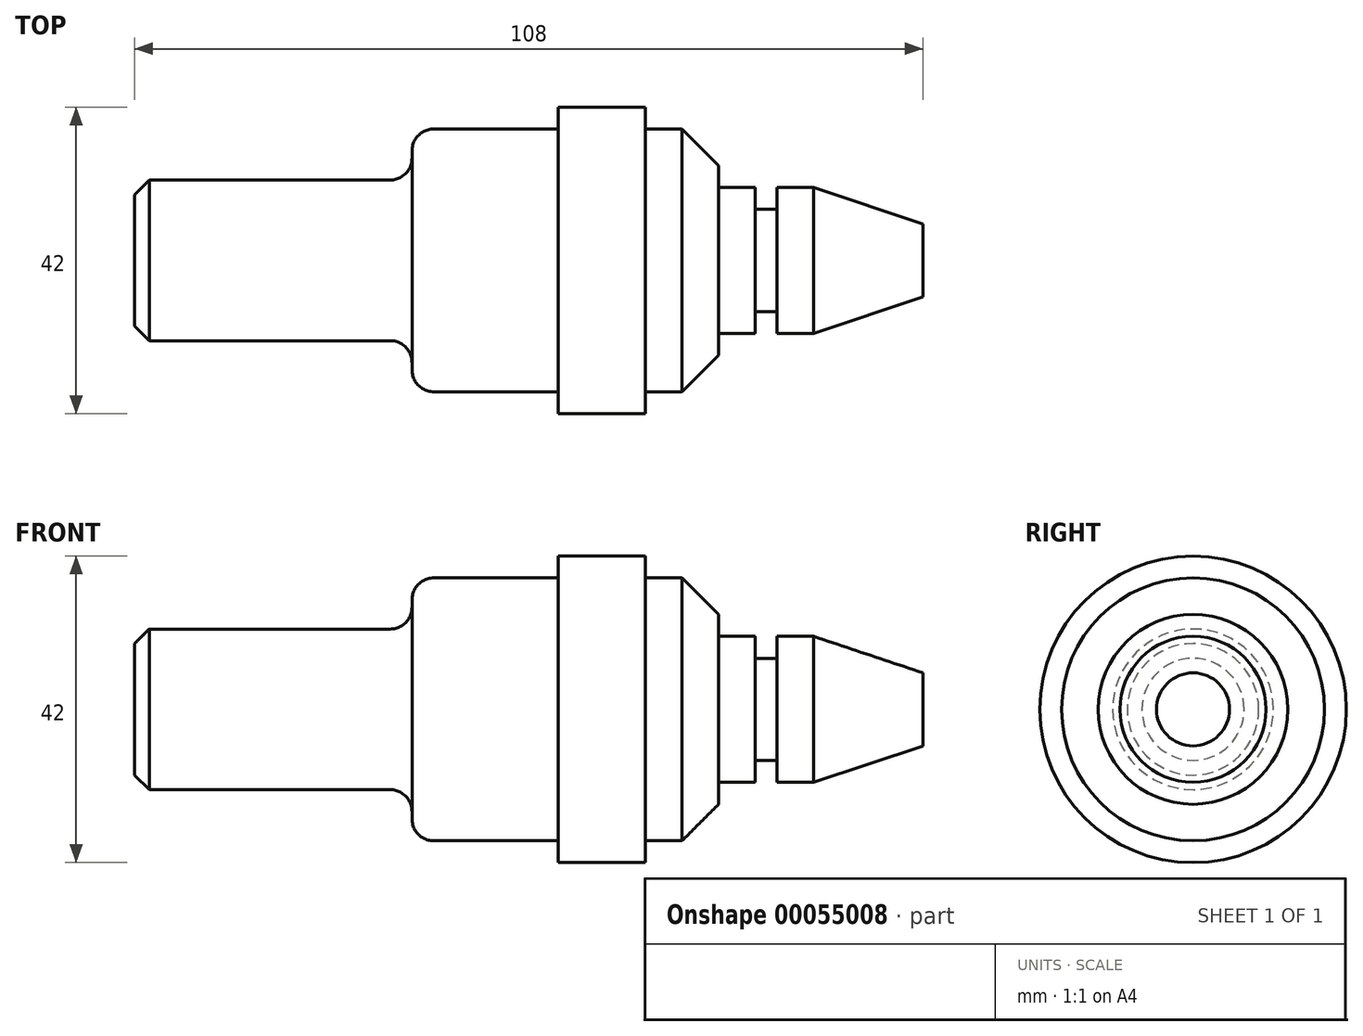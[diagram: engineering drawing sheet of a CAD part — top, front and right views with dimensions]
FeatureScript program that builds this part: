
annotation { "Feature Type Name" : "Feature", "Feature Type Description" : "" }
export const myFeature = defineFeature(function(context is Context, id is Id, definition is map)
    precondition{}
    {
        {
            var Q0;
            Q0=qCreatedBy(makeId("Top.planeOp"),FACE);
            var sketch = newSketch(context, id + "F0", { "sketchPlane" : qUnion([Q0])});
            skLineSegment(sketch, "E0", {"start": v(-39.66, 0) * mm, "end": v(68.34, 0) * mm});
            skLineSegment(sketch, "E1", {"start": v(-39.66, 0) * mm, "end": v(-39.66, -11) * mm});
            skLineSegment(sketch, "E2", {"start": v(-39.66, -11) * mm, "end": v(-1.66, -11) * mm});
            skLineSegment(sketch, "E3", {"start": v(-1.66, -11) * mm, "end": v(-1.66, -18) * mm});
            skLineSegment(sketch, "E4", {"start": v(-1.66, -18) * mm, "end": v(18.34, -18) * mm});
            skLineSegment(sketch, "E5", {"start": v(18.34, -18) * mm, "end": v(18.34, -21) * mm});
            skLineSegment(sketch, "E6", {"start": v(18.34, -21) * mm, "end": v(30.34, -21) * mm});
            skLineSegment(sketch, "E7", {"start": v(30.34, -21) * mm, "end": v(30.34, -18) * mm});
            skLineSegment(sketch, "E8", {"start": v(30.34, -18) * mm, "end": v(40.34, -18) * mm});
            skLineSegment(sketch, "E9", {"start": v(40.34, -18) * mm, "end": v(40.34, -10) * mm});
            skLineSegment(sketch, "E10", {"start": v(40.34, -10) * mm, "end": v(45.34, -10) * mm});
            skLineSegment(sketch, "E11", {"start": v(45.34, -10) * mm, "end": v(45.34, -7) * mm});
            skLineSegment(sketch, "E12", {"start": v(45.34, -7) * mm, "end": v(48.34, -7) * mm});
            skLineSegment(sketch, "E13", {"start": v(48.34, -7) * mm, "end": v(48.34, -10) * mm});
            skLineSegment(sketch, "E14", {"start": v(48.34, -10) * mm, "end": v(53.34, -10) * mm});
            skLineSegment(sketch, "E15", {"start": v(53.34, -10) * mm, "end": v(68.34, -5) * mm});
            skLineSegment(sketch, "E16", {"start": v(68.34, 0) * mm, "end": v(68.34, -5) * mm});
            skSolve(sketch);
        }
        {
            var Q0;
            Q0=makeQuery(id+"F0.imprint","IMPRINT",FACE,{"disambiguationData":[TD([[makeQuery(id+"F0.imprint","IMPRINT",EDGE,{"derivedFrom":sQuery(id+"F0.wireOp",EDGE,"E0")}),-1.0]])]});
            var Q1;
            Q1=sQuery(id+"F0.wireOp",EDGE,"E0");
            revolve(context, id + "F1", {"entities" : qUnion([Q0]), "axis" : qUnion([Q1]), "revolveType" : RevolveType.FULL});
        }
        {
            var Q0;
            Q0=makeQuery(id+"F1.opRevolve","SWEPT_EDGE",EDGE,{"disambiguationData":[OSD([sQuery(id+"F0.wireOp",EDGE,"E1"),sQuery(id+"F0.wireOp",EDGE,"E2")])]});
            chamfer(context, id + "F2", {"entities" : qUnion([Q0]), "chamferType" : ChamferType.OFFSET_ANGLE, "width" : 2 * mm, "oppositeDirection" : false, "angle" : 45 * degree, "tangentPropagation" : true});
        }
        {
            var Q0;
            Q0=makeQuery(id+"F1.opRevolve","SWEPT_EDGE",EDGE,{"disambiguationData":[OSD([sQuery(id+"F0.wireOp",EDGE,"E3"),sQuery(id+"F0.wireOp",EDGE,"E4")])]});
            var Q1;
            Q1=makeQuery(id+"F1.opRevolve","SWEPT_EDGE",EDGE,{"disambiguationData":[OSD([sQuery(id+"F0.wireOp",EDGE,"E2"),sQuery(id+"F0.wireOp",EDGE,"E3")])]});
            fillet(context, id + "F3", {"entities" : qUnion([Q0, Q1]), "radius" : 3 * mm, "tangentPropagation" : true, "allowEdgeOverflow" : false});
        }
        {
            var Q0;
            Q0=makeQuery(id+"F1.opRevolve","SWEPT_EDGE",EDGE,{"disambiguationData":[OSD([sQuery(id+"F0.wireOp",EDGE,"E8"),sQuery(id+"F0.wireOp",EDGE,"E9")])]});
            chamfer(context, id + "F4", {"entities" : qUnion([Q0]), "width" : 5 * mm, "tangentPropagation" : true});
        }
    });
